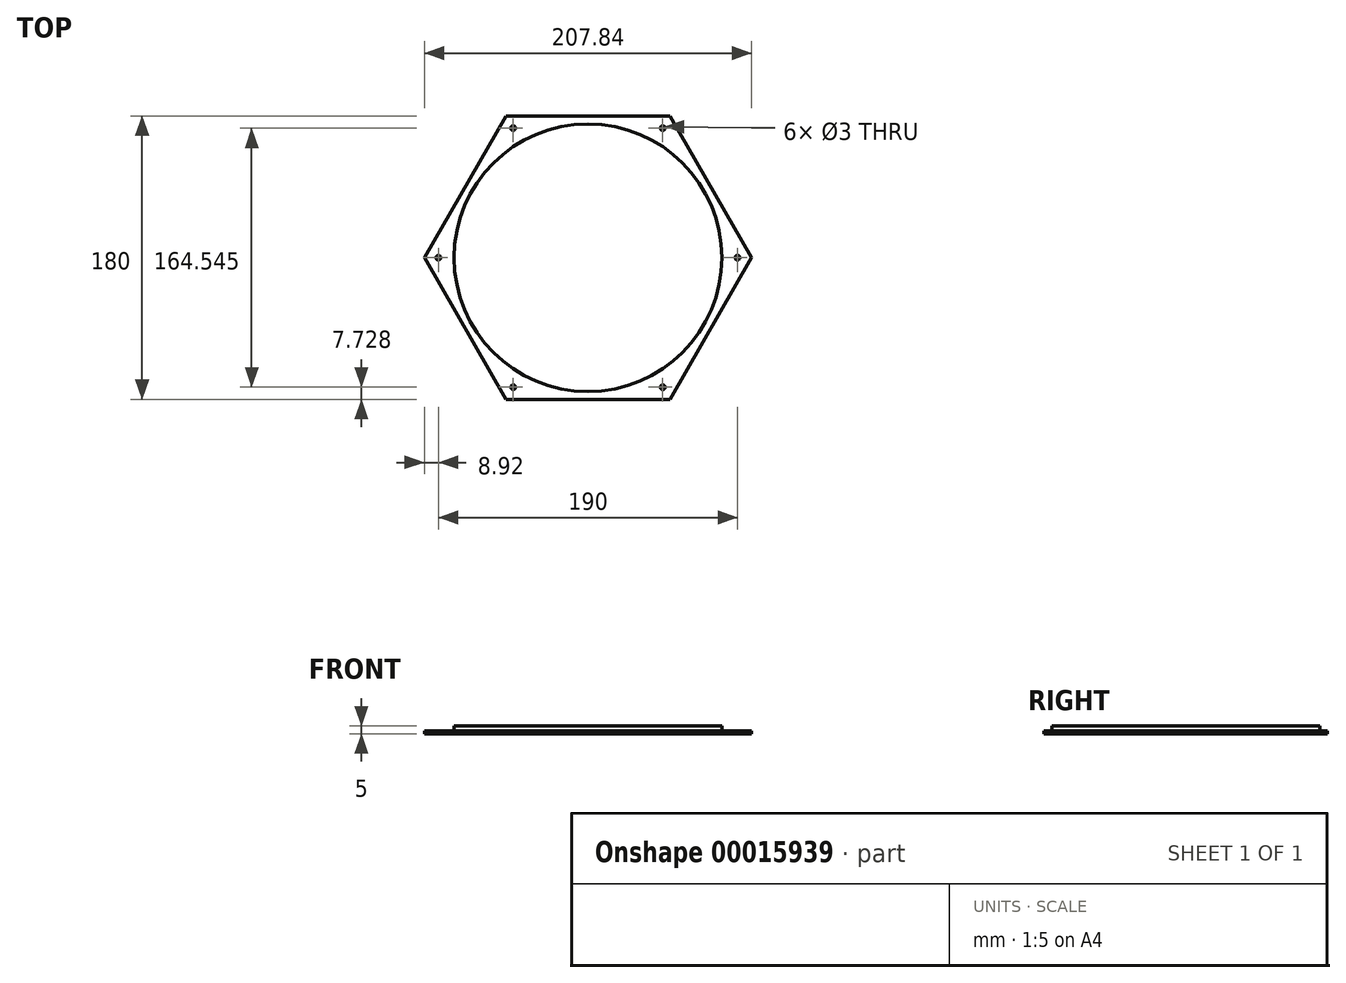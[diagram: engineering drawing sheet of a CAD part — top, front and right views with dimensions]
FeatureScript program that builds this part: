
annotation { "Feature Type Name" : "Feature", "Feature Type Description" : "" }
export const myFeature = defineFeature(function(context is Context, id is Id, definition is map)
    precondition{}
    {
        {
            var Q0;
            Q0=qCreatedBy(makeId("Top.planeOp"),FACE);
            var sketch = newSketch(context, id + "F0", { "sketchPlane" : qUnion([Q0])});
            skCircle(sketch, "E0", {"center": v(0, 0) * mm, "radius": 85 * mm});
            skCircle(sketch, "E1.cCircle", {"center": v(0, 0) * mm, "radius": 90 * mm, "construction": true});
            skLineSegment(sketch, "E1.0", {"start": v(-51.96, 90) * mm, "end": v(51.96, 90) * mm});
            skLineSegment(sketch, "E1.1", {"start": v(51.96, 90) * mm, "end": v(103.92, 0) * mm});
            skLineSegment(sketch, "E1.2", {"start": v(103.92, 0) * mm, "end": v(51.96, -90) * mm});
            skLineSegment(sketch, "E1.3", {"start": v(51.96, -90) * mm, "end": v(-51.96, -90) * mm});
            skLineSegment(sketch, "E1.4", {"start": v(-51.96, -90) * mm, "end": v(-103.92, 0) * mm});
            skLineSegment(sketch, "E1.5", {"start": v(-103.92, 0) * mm, "end": v(-51.96, 90) * mm});
            skSolve(sketch);
        }
        {
            var Q0;
            Q0=makeQuery(id+"F0.imprint","IMPRINT",FACE,{"disambiguationData":[TD([[makeQuery(id+"F0.imprint","IMPRINT",EDGE,{"derivedFrom":sQuery(id+"F0.wireOp",EDGE,"E0")}),1.0]])]});
            extrude(context, id + "F1", {"entities" : qUnion([Q0]), "depth" : 3 * mm});
        }
        {
            var Q0;
            Q0=makeQuery(id+"F0.imprint","IMPRINT",FACE,{"disambiguationData":[TD([[makeQuery(id+"F0.imprint","IMPRINT",EDGE,{"derivedFrom":sQuery(id+"F0.wireOp",EDGE,"E0")}),1.0]])]});
            var Q1;
            Q1=makeQuery(id+"F0.imprint","IMPRINT",FACE,{"disambiguationData":[TD([[makeQuery(id+"F0.imprint","IMPRINT",EDGE,{"derivedFrom":sQuery(id+"F0.wireOp",EDGE,"E0")}),-1.0]])]});
            extrude(context, id + "F2", {"entities" : qUnion([Q0, Q1]), "oppositeDirection" : true, "depth" : 2 * mm});
        }
        {
            var Q0;
            Q0=makeQuery(id+"F0.imprint","IMPRINT",FACE,{"disambiguationData":[TD([[makeQuery(id+"F0.imprint","IMPRINT",EDGE,{"derivedFrom":sQuery(id+"F0.wireOp",EDGE,"E0")}),-1.0]])]});
            var sketch = newSketch(context, id + "F3", { "sketchPlane" : qUnion([Q0])});
            skPoint(sketch, "E2", {"position": v(95, 0) * mm});
            skLineSegment(sketch, "E3", {"start": v(0, 0) * mm, "end": v(95, 0) * mm, "construction": true});
            skPoint(sketch, "E4.1.0", {"position": v(47.5, 82.27) * mm});
            skPoint(sketch, "E4.2.0", {"position": v(-47.5, 82.27) * mm});
            skPoint(sketch, "E4.3.0", {"position": v(-95, 0) * mm});
            skPoint(sketch, "E4.4.0", {"position": v(-47.5, -82.27) * mm});
            skPoint(sketch, "E4.5.0", {"position": v(47.5, -82.27) * mm});
            skPoint(sketch, "E4.center", {"position": v(0, 0) * mm});
            skSolve(sketch);
        }
        {
            var Q0;
            Q0=sQuery(id+"F3.wireOp",VERTEX,"E4.2.0");
            var Q1;
            Q1=sQuery(id+"F3.wireOp",VERTEX,"E4.1.0");
            var Q2;
            Q2=sQuery(id+"F3.wireOp",VERTEX,"E2");
            var Q3;
            Q3=sQuery(id+"F3.wireOp",VERTEX,"E4.5.0");
            var Q4;
            Q4=sQuery(id+"F3.wireOp",VERTEX,"E4.4.0");
            var Q5;
            Q5=sQuery(id+"F3.wireOp",VERTEX,"E4.3.0");
            var Q6;
            Q6=makeQuery(id+"F2.opExtrude","SWEPT_BODY",BODY,{"disambiguationData":[OSD([sQuery(id+"F0.wireOp",EDGE,"E1.0"),sQuery(id+"F0.wireOp",EDGE,"E1.1"),sQuery(id+"F0.wireOp",EDGE,"E1.2"),sQuery(id+"F0.wireOp",EDGE,"E1.3"),sQuery(id+"F0.wireOp",EDGE,"E1.4"),sQuery(id+"F0.wireOp",EDGE,"E1.5")])]});
            hole(context, id + "F4", {"style" : HoleStyle.SIMPLE, "endStyle" : HoleEndStyle.THROUGH, "holeDiameter" : 3 * mm, "locations" : qUnion([Q0, Q1, Q2, Q3, Q4, Q5]), "scope" : qUnion([Q6]), "isTappedThrough" : true, "startStyle" : HoleStartStyle.PART});
        }
    });
